# Revit family: Rohrschelle Trabant, M10-M12, Gummi
name_source: partatom
category: HLS-Bauteile
revit_build: Autodesk Revit 2017 (Build: 20190507_1515(x64)
units: mm (PartAtom-declared; Revit-internal decimal feet)

## family parameters
Arbeitsebenenbasiert = Ja
Beim Laden mit Abzugskörper schneiden = Nein
Bemaßung runder Anschluss = Durchmesser verwenden
Gemeinsam genutzt = Ja
Immer vertikal = Nein
Raumberechnungspunkt = Nein
Teiletyp = Normal

## types (5) — shared parameters
A = 29 mm
AB = 4 mm  [stored 0.0131234 ft]
Anschluss = M10/M12
Anschlußhöhe = 27 mm
Bauart = zweiteilig
Baustoffklasse = B2
DF1 = 17 mm
DF2 = 21 mm  [stored 0.0688976 ft]
DS = 5 mm  [stored 0.0164042 ft]
DVS = 5 mm  [stored 0.0164042 ft]
Dämmstärke = 5 mm  [stored 0.0164042 ft]
Fabrikat = MEFA
Farbe Schalldämmeinlage = schwarz
Firma = MEFA Befestigungs- und Montagesysteme GmbH
H1 = 2 mm  [stored 0.00656168 ft]
H2 = 6 mm  [stored 0.019685 ft]
HGA = 22 mm  [stored 0.0721785 ft]
Kurztext1 = Rohrschelle Trabant 25x2,5
MB = 25 mm  [stored 0.082021 ft]
MD = 3 mm  [stored 0.00984252 ft]
Material = Stahl
Material Schalldämmeinlage = EPDM
Materialmaße = 25x2,5 mm
Materialname = DD11
Mengeneinheit = St
Oberflaeche = galvanisch verzinkt
Schalldämmeinlage = Gummi
Verschluss = Rastverschluss
Verschluss-Schraube = M6
Vorgabe-Ansicht = 1219 mm
max. Temperaturbeständigkeit = 100 °C
max. zul. Last = 2.20 kN
max. zul. Last horizontal = 0.00 kN
max. zul. Last vertikal = 0.00 kN
vpe = 25 St
zero-valued in all types: Nennweite DN Rohr, Rohraußendurchmesser, Stärke Material

## per-type parameters (varying)
| type | Artikelnummer | B | Breite | D | D0 | Dmax | Dmin | EAN | Gewicht | Gewicht pro Bauteil | H | Kurztext2 | R | RM | Rohraußendurchmesser Zoll | S | max. Höhe | max. Rohraußendurchmesser | min. Rohraußendurchmesser |
| Trabant, Ø121-125, M10/M12, Gummi | 04272251 | 177 mm  [stored 0.580709 ft] | 176 mm  [stored 0.577428 ft] | 125 mm  [stored 0.410105 ft] | 134 mm | 125 mm  [stored 0.410105 ft] | 121 mm  [stored 0.396982 ft] | 4250928409300 | 0.31 kg | 0.31 kg | 161 mm  [stored 0.528215 ft] | 121 - 125 mm M10/M12 EPDM | 69 mm | 72 mm |  | 160 mm  [stored 0.524934 ft] | 162 mm  [stored 0.531496 ft] | 125 mm  [stored 0.410105 ft] | 121 mm  [stored 0.396982 ft] |
| Trabant, Ø132-136, M10/M12, Gummi | 04272361 | 188 mm | 187 mm | 136 mm | 145 mm | 136 mm | 132 mm  [stored 0.433071 ft] | 4250928409317 | 0.34 kg | 0.34 kg | 172 mm  [stored 0.564304 ft] | 132 - 136 mm M10/M12 EPDM | 75 mm | 77 mm  [stored 0.252625 ft] |  | 171 mm  [stored 0.561024 ft] | 173 mm  [stored 0.567585 ft] | 136 mm | 132 mm  [stored 0.433071 ft] |
| Trabant, Ø137-141, M10/M12, Gummi | 04272411 | 193 mm | 192 mm | 141 mm | 150 mm | 141 mm | 137 mm  [stored 0.449475 ft] | 4250928409324 | 0.34 kg | 0.34 kg | 177 mm  [stored 0.580709 ft] | 137 - 141 mm M10/M12 EPDM | 77 mm  [stored 0.252625 ft] | 80 mm | 5 Zoll | 176 mm  [stored 0.577428 ft] | 178 mm | 141 mm | 137 mm  [stored 0.449475 ft] |
| Trabant, Ø159-163, M10/M12, Gummi | 04272631 | 215 mm | 215 mm | 163 mm  [stored 0.534777 ft] | 172 mm  [stored 0.564304 ft] | 163 mm  [stored 0.534777 ft] | 159 mm  [stored 0.521654 ft] | 4250928409331 | 0.39 kg | 0.39 kg | 199 mm | 159 - 163 mm M10/M12 EPDM | 88 mm  [stored 0.288714 ft] | 91 mm |  | 198 mm | 200 mm | 163 mm  [stored 0.534777 ft] | 159 mm  [stored 0.521654 ft] |
| Trabant, Ø164-168, M10/M12, Gummi | 04272681 | 220 mm | 220 mm | 168 mm  [stored 0.551181 ft] | 177 mm  [stored 0.580709 ft] | 168 mm  [stored 0.551181 ft] | 164 mm  [stored 0.538058 ft] | 4250928409348 | 0.40 kg | 0.40 kg | 204 mm | 164 - 168 mm M10/M12 EPDM | 91 mm | 93 mm  [stored 0.305118 ft] | 6 Zoll | 203 mm | 205 mm | 168 mm  [stored 0.551181 ft] | 164 mm  [stored 0.538058 ft] |

note: [stored X ft] marks values corroborated as IEEE doubles in the binary element streams (Revit-internal decimal feet)

## geometry (parser evidence)
native form markers: Sweep x1
no freeform markers — native parametric forms only
